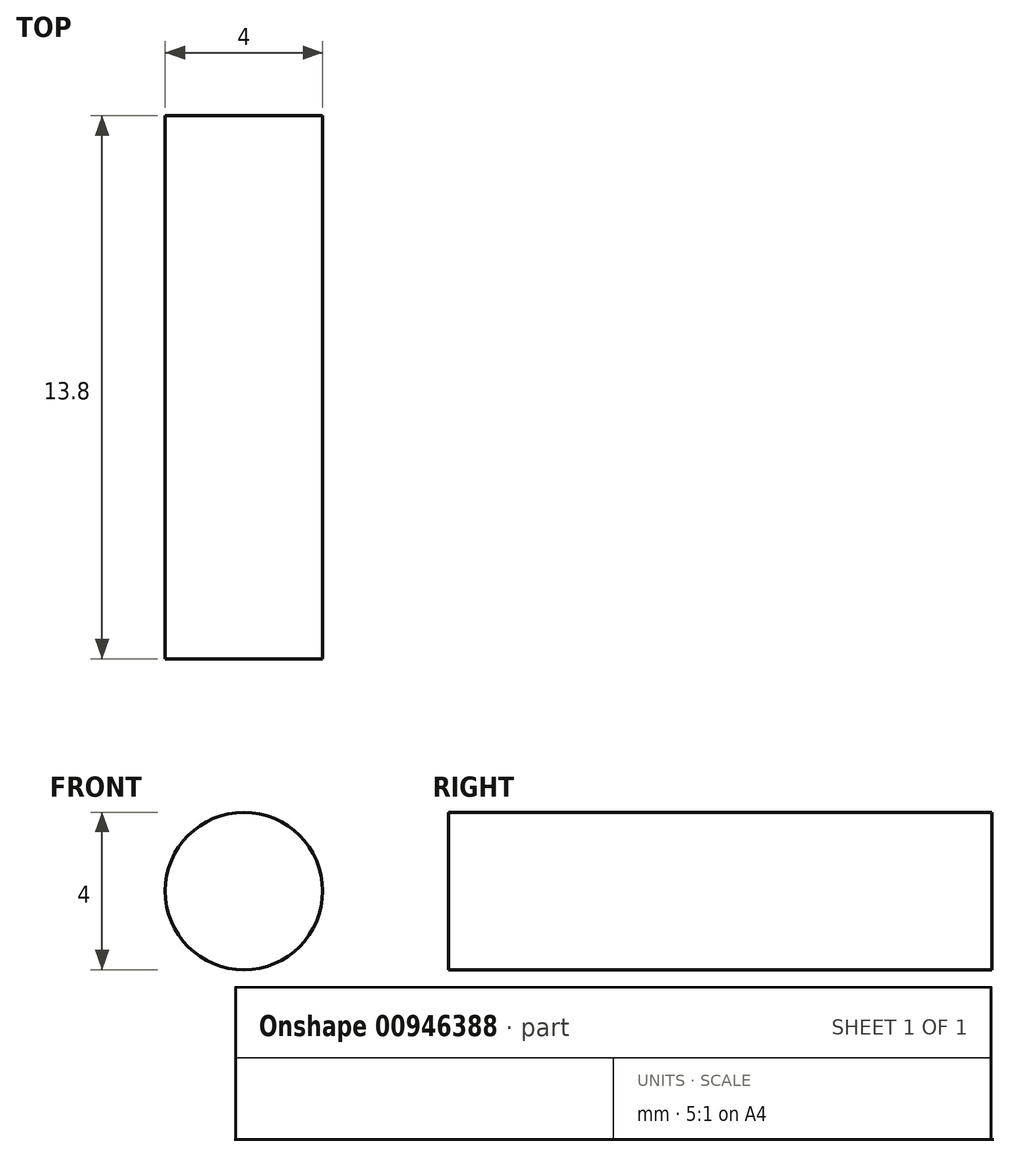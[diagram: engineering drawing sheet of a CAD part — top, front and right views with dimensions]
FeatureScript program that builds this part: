
annotation { "Feature Type Name" : "Feature", "Feature Type Description" : "" }
export const myFeature = defineFeature(function(context is Context, id is Id, definition is map)
    precondition{}
    {
        {
            var Q0;
            Q0=qCreatedBy(makeId("Front.planeOp"),FACE);
            var sketch = newSketch(context, id + "F0", { "sketchPlane" : qUnion([Q0])});
            skCircle(sketch, "E0", {"center": v(0, 0) * mm, "radius": 2 * mm});
            skSolve(sketch);
        }
        {
            var Q0;
            Q0=qSketchRegion(id+"F0",true);
            extrude(context, id + "F1", {"entities" : qUnion([Q0]), "endBound" : BoundingType.SYMMETRIC, "depth" : 13.8 * mm, "offsetDistance" : 25 * mm});
        }
    });
